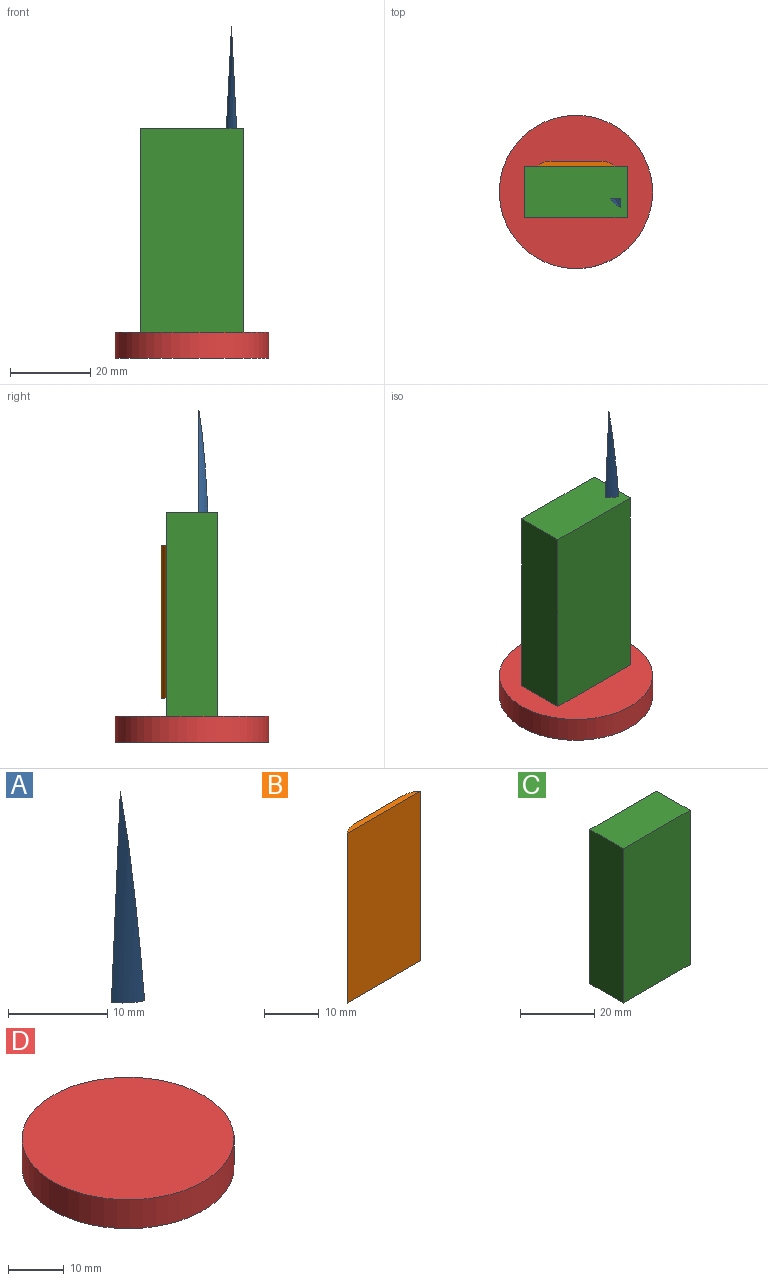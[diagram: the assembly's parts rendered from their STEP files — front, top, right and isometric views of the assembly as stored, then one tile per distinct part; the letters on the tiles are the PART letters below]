
ASSEMBLY  parts=4 mates=2
PART A: 4 faces, bbox 3.8x2.2x25.5 mm
  f0: plane 2.56x2.2mm, normal (0,0,-1), area 3.4mm2, adj f1,f2,f3
  f1: plane 25.37x2.19mm, normal (1,0,0.05), area 34.1mm2, adj f0,f2,f3
  f2: plane 25.37x2.54mm, normal (0,1,0), area 32.2mm2, adj f0,f1,f3
  f3: cylinder r=5.08mm len=25.5mm, axis (0.05,0,1), area 47.5mm2, adj f0,f1,f2
PART B: 6 faces, bbox 19.1x1.3x38.1 mm
  f0: plane 19.05x1.27mm, normal (0,0,-1), area 21.5mm2, adj f2,f3,f4,f5
  f1: plane 19.05x1.27mm, normal (0,0,1), area 21.5mm2, adj f2,f3,f4,f5
  f2: plane 38.1x12.33mm, normal (0,1,0), area 469.8mm2, adj f0,f1,f4,f5
  f3: plane 38.1x19.05mm, normal (0,-1,0), area 725.8mm2, adj f0,f1,f4,f5
  f4: cylinder r=5.08mm len=38.1mm, axis (0,0,-1), area 139.9mm2, adj f0,f1,f2,f3
  f5: cylinder r=5.08mm len=38.1mm, axis (0,0,-1), area 139.9mm2, adj f0,f1,f2,f3
PART C: 6 faces, bbox 25.4x12.7x50.8 mm
  f0: plane 25.4x12.7mm, normal (0,0,-1), area 322.6mm2, adj f1,f3,f4,f5
  f1: plane 50.8x12.7mm, normal (1,0,0), area 645.2mm2, adj f0,f2,f4,f5
  f2: plane 25.4x12.7mm, normal (0,0,1), area 322.6mm2, adj f1,f3,f4,f5
  f3: plane 50.8x12.7mm, normal (-1,0,0), area 645.2mm2, adj f0,f2,f4,f5
  f4: plane 50.8x25.4mm, normal (0,-1,0), area 1290.3mm2, adj f0,f1,f2,f3
  f5: plane 50.8x25.4mm, normal (0,1,0), area 1290.3mm2, adj f0,f1,f2,f3
PART D: 3 faces, bbox 38.1x38.1x6.4 mm
  f0: cylinder r=19.05mm len=38.1mm, axis (0,0,-1), area 760.1mm2, adj f1,f2
  f1: plane 38.1x38.1mm, normal (0,0,1), area 1140.1mm2, adj f0
  f2: plane 38.1x38.1mm, normal (0,0,-1), area 1140.1mm2, adj f0
PLACE A t=(9.83,-8.08,7.58)mm
PLACE B at identity
PLACE C at identity fixed
PLACE D t=(0,-6.35,-29.87)mm
MATE fastened C.f0 <-> D.f0  axis (0,0,-1) through (0,-6.35,-23.52)mm
MATE slider C.f2 <-> A.f0  axis (0,0,1) through (0,-6.35,27.28)mm
